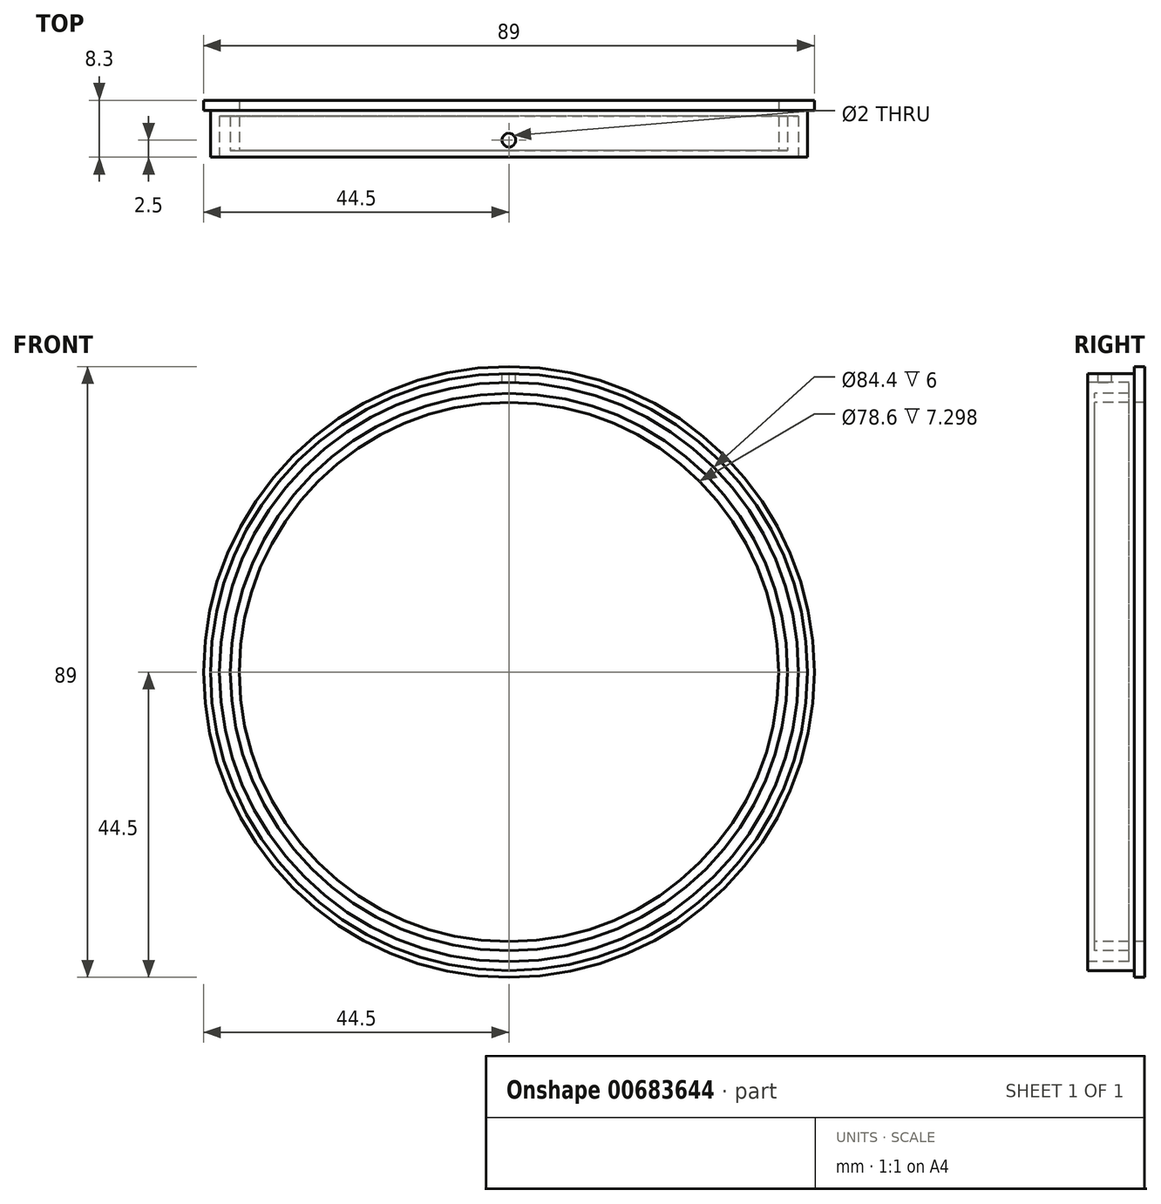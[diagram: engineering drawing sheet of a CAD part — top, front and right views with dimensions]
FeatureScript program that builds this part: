
annotation { "Feature Type Name" : "Feature", "Feature Type Description" : "" }
export const myFeature = defineFeature(function(context is Context, id is Id, definition is map)
    precondition{}
    {
        {
            var Q0;
            Q0=qCreatedBy(makeId("Right.planeOp"),FACE);
            var sketch = newSketch(context, id + "F0", { "sketchPlane" : qUnion([Q0])});
            skLineSegment(sketch, "E0", {"start": v(-32.34, 0) * mm, "end": v(38.37, 0) * mm, "construction": true});
            skLineSegment(sketch, "E1", {"start": v(0, 0) * mm, "end": v(0, -39.3) * mm, "construction": true});
            skLineSegment(sketch, "E2", {"start": v(0, -39.3) * mm, "end": v(0, -44.5) * mm});
            skLineSegment(sketch, "E3", {"start": v(0, -44.5) * mm, "end": v(-1.5, -44.5) * mm});
            skLineSegment(sketch, "E4", {"start": v(-1.5, -44.5) * mm, "end": v(-1.5, -43.5) * mm});
            skLineSegment(sketch, "E5", {"start": v(-1.5, -43.5) * mm, "end": v(-8.3, -43.5) * mm});
            skLineSegment(sketch, "E6", {"start": v(-8.3, -43.5) * mm, "end": v(-8.3, -42.2) * mm});
            skLineSegment(sketch, "E7", {"start": v(-8.3, -42.2) * mm, "end": v(-2.3, -42.2) * mm});
            skLineSegment(sketch, "E8", {"start": v(-2.3, -42.2) * mm, "end": v(-2.3, -40.6) * mm});
            skLineSegment(sketch, "E9", {"start": v(-2.3, -40.6) * mm, "end": v(-7.3, -40.6) * mm});
            skLineSegment(sketch, "E10", {"start": v(-7.3, -40.6) * mm, "end": v(-7.3, -39.3) * mm});
            skLineSegment(sketch, "E11", {"start": v(-7.3, -39.3) * mm, "end": v(0, -39.3) * mm});
            skSolve(sketch);
        }
        {
            var Q0;
            Q0=makeQuery(id+"F0.imprint","IMPRINT",FACE,{"disambiguationData":[TD([[makeQuery(id+"F0.imprint","IMPRINT",EDGE,{"derivedFrom":sQuery(id+"F0.wireOp",EDGE,"E2")}),-1.0]])]});
            var Q1;
            Q1=sQuery(id+"F0.wireOp",EDGE,"E0");
            revolve(context, id + "F1", {"entities" : qUnion([Q0]), "axis" : qUnion([Q1]), "revolveType" : RevolveType.FULL});
        }
        {
            var Q0;
            Q0=qCreatedBy(makeId("Top.planeOp"),FACE);
            cPlane(context, id + "F2", {"entities" : qUnion([Q0]), "cplaneType" : CPlaneType.OFFSET, "offset" : 44 * mm, "width" : 150 * mm, "height" : 150 * mm});
        }
        {
            var Q0;
            Q0=qCreatedBy(id+"F2.planeOp",FACE);
            var sketch = newSketch(context, id + "F3", { "sketchPlane" : qUnion([Q0])});
            skPoint(sketch, "E12", {"position": v(0, -5.8) * mm});
            skSolve(sketch);
        }
        {
            var Q0;
            Q0=sQuery(id+"F3.wireOp",VERTEX,"E12");
            var Q1;
            Q1=makeQuery(id+"F1.opRevolve","SWEPT_BODY",BODY,{"disambiguationData":[OSD([sQuery(id+"F0.wireOp",EDGE,"E2"),sQuery(id+"F0.wireOp",EDGE,"E3"),sQuery(id+"F0.wireOp",EDGE,"E4"),sQuery(id+"F0.wireOp",EDGE,"E5"),sQuery(id+"F0.wireOp",EDGE,"E6"),sQuery(id+"F0.wireOp",EDGE,"E7"),sQuery(id+"F0.wireOp",EDGE,"E8"),sQuery(id+"F0.wireOp",EDGE,"E9"),sQuery(id+"F0.wireOp",EDGE,"E10"),sQuery(id+"F0.wireOp",EDGE,"E11")])]});
            hole(context, id + "F4", {"style" : HoleStyle.SIMPLE, "endStyle" : HoleEndStyle.BLIND, "holeDiameter" : 2 * mm, "majorDiameter" : 5 * mm, "holeDepth" : 2.2 * mm, "tappedDepth" : 12 * mm, "tapClearance" : 3, "locations" : qUnion([Q0]), "scope" : qUnion([Q1])});
        }
    });
